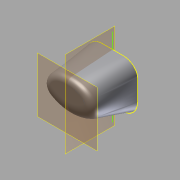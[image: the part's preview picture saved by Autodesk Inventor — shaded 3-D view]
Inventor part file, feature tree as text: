
AUTODESK INVENTOR PART (.ipt)
format: ipt  version: 2012 (Build 160160000, 160)  size: 455,680 bytes
history: native  units: in
note: dims shown in document units (in); Inventor stores cm internally (conversion verified against a paired STEP export)
features: sketch x8, fillet x4, plane x3, extrude x3, loft x1, revolve x1
ambient origin geometry x8: Origin, YZ Plane, XZ Plane, XY Plane, X Axis, Y Axis, Z Axis, Center Point
bodies: Solid1 (feature_tree)
feature tree (20):
  sketch  "Sketch1"  dims[d0=3.45in d1=3.8075in]
  plane  "Work Plane2"
  loft  "Loft1"
  sketch  "Sketch5"  dims[d4=3.4895in d6=2.53in]
  plane  "Work Plane4"
  revolve  "Revolution1"  [1 undecoded]
  extrude  "Extrusion1"  Depth=2.53in
  sketch  "Sketch9"  dims[d34=2.4755in]
  extrude  "Extrusion2"  TaperAngle=0.0deg  [1 undecoded]
  extrude  "Extrusion3"  TaperAngle=180.0deg  [1 undecoded]
  fillet  "Fillet6"  Radius=5.0in
  fillet  "Fillet8"  Radius=1.047in
  fillet  "Fillet9"  Radius=0.5235in
  fillet  "Fillet11"  Radius=1.047in
  plane  "Work Plane1"
  sketch  "Sketch2"  dims[d2=1.6885in d3=2.766in]
  sketch  "Sketch6"  dims[d8=0.0in d10=0.0in d11=90.0deg]
  sketch  "Sketch7"  dims[d12=0.0in d13=90.0deg d19=180.0deg d20=5.0in d21=0.0in d31=1.047in d32=0.5235in d33=1.047in]
  sketch  "Sketch10"  dims[d42=0.4745in]
  sketch  "Sketch11"  dims[d43=1.047in d44=0.0in d45=2.4755in d46=0.0in d49=0.5445in d50=2.4755in d51=0.0in d52=0.125in d54=1.6885in d55=1.6885in d58=1.6885in d59=0.8443in d60=1.9811in d61=0.25in d62=90.0deg d63=0.5235in d64=0.125in d65=0.8in d66=0.8in d67=0.4in d68=0.2047in d73=0.0in d74=0.0in d75=1.0in d76=0.1969in]
note: 3 required parameter values undecoded (feature->parameter linkage not recoverable at this tier; creation-order binding heuristic only, values carry confidence <= 0.55)